# Revit family: Division_Twelve-Twigz-Rectangular_Café_Table-1
name_source: partatom
category: Furniture
units: mm (PartAtom-declared; Revit-internal decimal feet)

## family parameters
Always vertical = Yes
Cut with Voids When Loaded = No
OmniClass Number = 23.40.20.00
OmniClass Title = General Furniture and Specialties
Room Calculation Point = No
Shared = No
Work Plane-Based = No

## types (6) — shared parameters
Assembly Code = E2020200
Default Elevation = 0"
Depth = 32"
Keynote = 12500
Low Emitting Finish = Yes
Low Emitting Material = Yes
Manufacturer = Division Twelve
Product Documentation Link = https://division12.com
Revit Model Built By = https://servex-us.com
Salvage or Reuse = Yes
Type Comments = Twigz
URL = https://division12.com
zero-valued in all types: Percentage of Recycled Content

## per-type parameters (varying)
| type | Description | Height | T-1 | T-2 | Width |
| 115406A | Rectangular 32" x 93" café table with white oak top | 29 1/8" | Yes | No | 93" |
| 115406F | Rectangular 32" x 93" café table with stained oak top | 29 1/8" | Yes | No | 93" |
| 115406G | Rectangular 32” x 93” café table with outdoor laminate top | 28 7/8" | No | Yes | 93" |
| 115407A | Rectangular 32" x 69" café table with white oak top | 29 1/8" | Yes | No | 69" |
| 115407F | Rectangular 32" x 69" café table with stained oak top | 29 1/8" | Yes | No | 69" |
| 115407G | Rectangular 32” x 69" café table with outdoor laminate top | 28 7/8" | No | Yes | 69" |

note: column(s) folded — value = type name in every type: Model

## geometry (parser evidence)
native form markers: Sweep x3
no freeform markers — native parametric forms only
